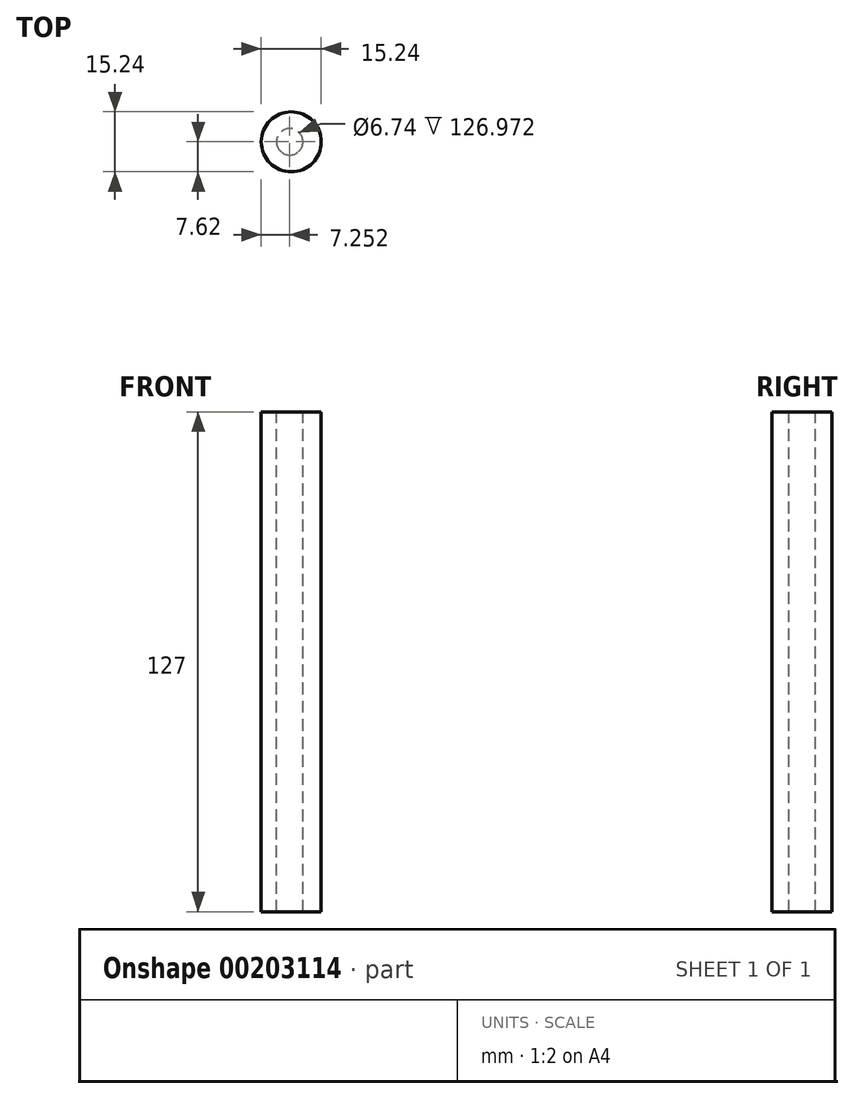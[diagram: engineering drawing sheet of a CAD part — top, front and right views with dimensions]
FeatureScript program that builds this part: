
annotation { "Feature Type Name" : "Feature", "Feature Type Description" : "" }
export const myFeature = defineFeature(function(context is Context, id is Id, definition is map)
    precondition{}
    {
        {
            var Q0;
            Q0=qCreatedBy(makeId("Front.planeOp"),FACE);
            var sketch = newSketch(context, id + "F0", { "sketchPlane" : qUnion([Q0])});
            skLineSegment(sketch, "E0.bottom", {"start": v(-20.35, 68.46) * mm, "end": v(-12.73, 68.46) * mm});
            skLineSegment(sketch, "E0.top", {"start": v(-20.35, -58.54) * mm, "end": v(-12.73, -58.54) * mm});
            skLineSegment(sketch, "E0.left", {"start": v(-20.35, 68.46) * mm, "end": v(-20.35, -58.54) * mm});
            skLineSegment(sketch, "E0.right", {"start": v(-12.73, 68.46) * mm, "end": v(-12.73, -58.54) * mm});
            skSolve(sketch);
        }
        {
            var Q0;
            Q0 = qSketchRegion(id + "F0", true);
            var Q1;
            Q1=sQuery(id+"F0.wireOp",EDGE,"E0.right");
            revolve(context, id + "F1", {"entities" : qUnion([Q0]), "axis" : qUnion([Q1]), "revolveType" : RevolveType.FULL});
        }
        {
            var Q0;
            Q0=qCreatedBy(makeId("Front.planeOp"),FACE);
            var sketch = newSketch(context, id + "F2", { "sketchPlane" : qUnion([Q0])});
            skLineSegment(sketch, "E1.bottom", {"start": v(-13.1, 68.43) * mm, "end": v(-16.47, 68.43) * mm});
            skLineSegment(sketch, "E1.top", {"start": v(-13.1, -58.57) * mm, "end": v(-16.47, -58.57) * mm});
            skLineSegment(sketch, "E1.left", {"start": v(-13.1, 68.43) * mm, "end": v(-13.1, -58.57) * mm});
            skLineSegment(sketch, "E1.right", {"start": v(-16.47, 68.43) * mm, "end": v(-16.47, -58.57) * mm});
            skSolve(sketch);
        }
        {
            var Q0;
            Q0 = qSketchRegion(id + "F2", true);
            var Q1;
            Q1=sQuery(id+"F2.wireOp",EDGE,"E1.left");
            revolve(context, id + "F3", {"operationType" : NewBodyOperationType.REMOVE, "entities" : qUnion([Q0]), "axis" : qUnion([Q1]), "revolveType" : RevolveType.FULL});
        }
    });
